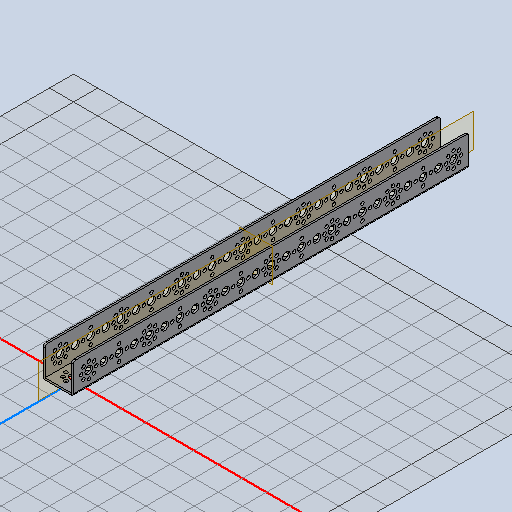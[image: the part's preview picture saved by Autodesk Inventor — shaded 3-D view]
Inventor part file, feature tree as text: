
AUTODESK INVENTOR PART (.ipt)
format: ipt  version: 2022 (Build 260153000, 153)  size: 642,560 bytes
history: native  units: in
note: dims shown in document units (in); Inventor stores cm internally (conversion verified against a paired STEP export)
features: other x216, plane x2, imported_body x1
ambient origin geometry x8: Origin, YZ Plane, XZ Plane, XY Plane, X Axis, Y Axis, Z Axis, Center Point
bodies: Body1 (feature_tree)
feature tree (219):
  other  "tetrix_739069_2012"
  other  "tetrix_739069_20121"
  other  "A_1"
  other  "A_78"
  other  "A_79"
  other  "A_80"
  other  "A_81"
  other  "A_82"
  other  "A_83"
  other  "A_84"
  other  "A_85"
  other  "A_27"
  other  "A_86"
  other  "A_87"
  other  "A_88"
  other  "A_89"
  other  "A_90"
  other  "A_91"
  other  "A_92"
  other  "A_93"
  other  "A_119"
  other  "A_120"
  other  "A_121"
  other  "A_122"
  other  "A_123"
  other  "A_124"
  other  "A_125"
  other  "A_126"
  other  "A_127"
  other  "A_149"
  other  "A_150"
  other  "A_151"
  other  "A_152"
  other  "A_153"
  other  "A_154"
  other  "A_155"
  other  "A_156"
  other  "A_157"
  other  "A_158"
  other  "A_159"
  other  "A_160"
  other  "A_161"
  other  "A_162"
  other  "A_163"
  other  "A_164"
  other  "A_165"
  other  "A_166"
  other  "Work Axis46"
  other  "Work Axis47"
  other  "Work Axis48"
  other  "Work Axis49"
  other  "Work Axis50"
  other  "Work Axis51"
  other  "Work Axis52"
  other  "Work Axis53"
  other  "Work Axis54"
  other  "Work Axis55"
  other  "Work Axis56"
  other  "Work Axis57"
  other  "Work Axis58"
  other  "Work Axis59"
  other  "Work Axis60"
  other  "Work Axis61"
  other  "Work Axis62"
  other  "Work Axis63"
  other  "A_18"
  other  "A_94"
  other  "A_95"
  other  "A_96"
  other  "A_97"
  other  "A_98"
  other  "A_99"
  other  "A_100"
  other  "A_101"
  other  "A_31"
  other  "A_102"
  other  "A_103"
  other  "A_104"
  other  "A_105"
  other  "A_106"
  other  "A_107"
  other  "A_108"
  other  "A_109"
  other  "A_128"
  other  "A_129"
  other  "A_130"
  other  "A_131"
  other  "A_132"
  other  "A_133"
  other  "A_134"
  other  "A_135"
  other  "A_136"
  other  "A_1283"
  other  "A_1284"
  other  "A_1285"
  other  "A_1286"
  other  "A_1287"
  other  "A_1288"
  other  "A_1289"
  other  "A_1290"
  other  "A_1291"
  other  "A_1292"
  other  "A_1293"
  other  "A_1294"
  other  "A_1295"
  other  "A_1296"
  other  "A_1297"
  other  "A_1298"
  other  "A_1299"
  other  "A_1300"
  other  "Work Axis109"
  other  "Work Axis110"
  other  "Work Axis111"
  other  "Work Axis112"
  other  "Work Axis113"
  other  "Work Axis114"
  other  "Work Axis115"
  other  "Work Axis116"
  other  "Work Axis117"
  other  "Work Axis118"
  other  "Work Axis119"
  other  "Work Axis120"
  other  "Work Axis121"
  other  "Work Axis122"
  other  "Work Axis123"
  other  "Work Axis124"
  other  "Work Axis125"
  other  "Work Axis126"
  other  "A_77"
  other  "A_110"
  other  "A_111"
  other  "A_112"
  other  "A_113"
  other  "A_139"
  other  "A_140"
  other  "A_141"
  other  "A_142"
  other  "A_143"
  other  "A_2421"
  other  "A_2422"
  other  "A_2423"
  other  "A_2424"
  other  "A_2425"
  other  "A_2426"
  other  "A_2427"
  other  "A_2428"
  other  "A_2429"
  other  "A_2430"
  other  "A_2449"
  other  "A_2450"
  other  "A_2451"
  other  "A_2452"
  other  "A_2453"
  other  "A_2454"
  other  "A_2455"
  other  "A_2456"
  other  "A_2457"
  other  "A_2458"
  other  "A_114"
  other  "A_115"
  other  "A_116"
  other  "A_117"
  other  "A_118"
  other  "A_144"
  other  "A_145"
  other  "A_146"
  other  "A_147"
  other  "A_148"
  other  "A_2431"
  other  "A_2432"
  other  "A_2433"
  other  "A_2434"
  other  "A_2435"
  other  "A_2436"
  other  "A_2437"
  other  "A_2438"
  other  "A_2439"
  other  "A_2440"
  other  "A_2459"
  other  "A_2460"
  other  "A_2461"
  other  "A_2462"
  other  "A_2463"
  other  "A_2464"
  other  "A_2465"
  other  "A_2466"
  other  "A_2467"
  other  "A_2468"
  other  "A_75"
  other  "A_76"
  other  "A_137"
  other  "A_138"
  other  "A_2441"
  other  "A_2442"
  other  "A_2443"
  other  "A_2444"
  other  "A_2469"
  other  "A_2470"
  other  "A_2471"
  other  "A_2472"
  other  "A_2417"
  other  "A_2418"
  other  "A_2419"
  other  "A_2420"
  other  "A_2445"
  other  "A_2446"
  other  "A_2447"
  other  "A_2448"
  other  "A_2473"
  other  "A_2474"
  other  "A_2475"
  other  "A_2476"
  other  "FRONT"
  other  "TOP"
  other  "RIGHT"
  other  "DTM1"
  plane  "Work Plane5"
  plane  "Work Plane6"
  imported_body  "Base1"
